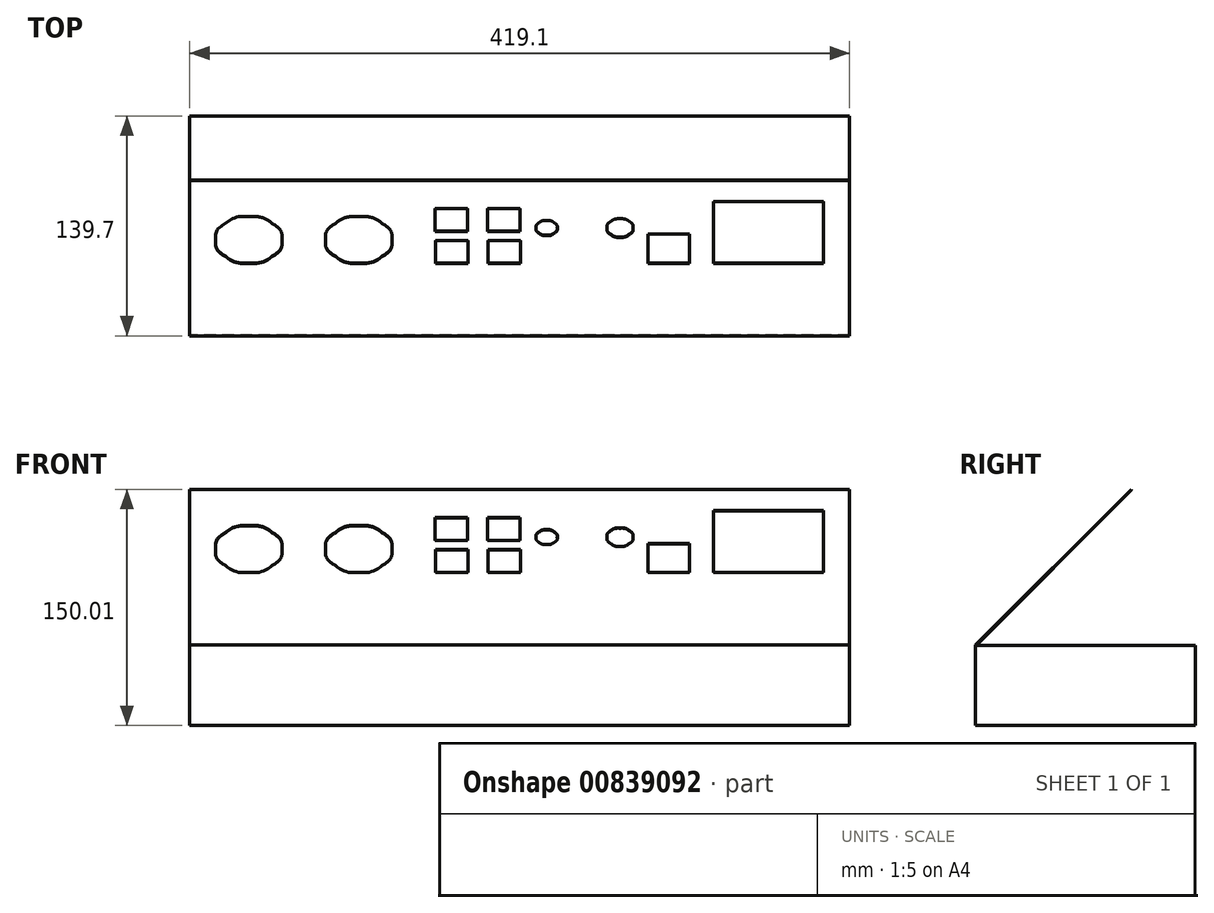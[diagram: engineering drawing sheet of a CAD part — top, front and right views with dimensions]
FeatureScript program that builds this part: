
annotation { "Feature Type Name" : "Feature", "Feature Type Description" : "" }
export const myFeature = defineFeature(function(context is Context, id is Id, definition is map)
    precondition{}
    {
        {
            var Q0;
            Q0=qCreatedBy(makeId("Right.planeOp"),FACE);
            var sketch = newSketch(context, id + "F0", { "sketchPlane" : qUnion([Q0])});
            skLineSegment(sketch, "E0.bottom", {"start": v(0, 0) * mm, "end": v(-139.7, 0) * mm});
            skLineSegment(sketch, "E0.top", {"start": v(0, 50.8) * mm, "end": v(-139.3, 50.8) * mm});
            skLineSegment(sketch, "E0.left", {"start": v(0, 0) * mm, "end": v(0, 50.8) * mm});
            skLineSegment(sketch, "E0.right", {"start": v(-139.7, 0) * mm, "end": v(-139.7, 51.22) * mm});
            skLineSegment(sketch, "E1", {"start": v(-139.7, 51.22) * mm, "end": v(-40.92, 150) * mm});
            skLineSegment(sketch, "E2", {"start": v(-40.92, 150) * mm, "end": v(-40.63, 149.72) * mm});
            skLineSegment(sketch, "E3", {"start": v(-40.63, 149.72) * mm, "end": v(-139.3, 51.05) * mm});
            skLineSegment(sketch, "E4", {"start": v(-139.3, 50.8) * mm, "end": v(-139.3, 51.05) * mm});
            skLineSegment(sketch, "E5", {"start": v(-139.3, 50.8) * mm, "end": v(-139.7, 50.8) * mm, "construction": true});
            skSolve(sketch);
        }
        {
            var Q0;
            Q0=qSketchRegion(id+"F0",true);
            extrude(context, id + "F1", {"entities" : qUnion([Q0]), "endBound" : BoundingType.SYMMETRIC, "depth" : 419.1 * mm, "offsetDistance" : 25.4 * mm});
        }
        {
            var Q0;
            Q0=makeQuery(id+"F1.opExtrude","SWEPT_FACE",FACE,{"disambiguationData":[OSD([sQuery(id+"F0.wireOp",EDGE,"E1")])]});
            var sketch = newSketch(context, id + "F2", { "sketchPlane" : qUnion([Q0])});
            skLineSegment(sketch, "E6", {"start": v(-32.8, 2.55) * mm, "end": v(-32.8, 23.19) * mm});
            skLineSegment(sketch, "E7", {"start": v(-32.8, 23.19) * mm, "end": v(-53.43, 23.19) * mm});
            skLineSegment(sketch, "E8", {"start": v(-53.43, 2.55) * mm, "end": v(-53.43, 23.19) * mm});
            skLineSegment(sketch, "E9", {"start": v(-53.43, 2.55) * mm, "end": v(-32.8, 2.55) * mm});
            skLineSegment(sketch, "E10", {"start": v(-53.83, 31.12) * mm, "end": v(-53.83, 51.76) * mm});
            skLineSegment(sketch, "E11", {"start": v(-53.83, 31.12) * mm, "end": v(-33.2, 31.12) * mm});
            skLineSegment(sketch, "E12", {"start": v(-33.2, 51.76) * mm, "end": v(-53.83, 51.76) * mm});
            skLineSegment(sketch, "E13", {"start": v(-33.2, 31.12) * mm, "end": v(-33.2, 51.76) * mm});
            skLineSegment(sketch, "E14", {"start": v(-20.1, 2.55) * mm, "end": v(0.54, 2.55) * mm});
            skLineSegment(sketch, "E15", {"start": v(-20.1, 2.55) * mm, "end": v(-20.1, 23.19) * mm});
            skLineSegment(sketch, "E16", {"start": v(0.54, 23.19) * mm, "end": v(-20.1, 23.19) * mm});
            skLineSegment(sketch, "E17", {"start": v(0.54, 2.55) * mm, "end": v(0.54, 23.19) * mm});
            skLineSegment(sketch, "E18", {"start": v(0.15, 31.12) * mm, "end": v(0.15, 51.76) * mm});
            skLineSegment(sketch, "E19", {"start": v(0.15, 51.76) * mm, "end": v(-20.5, 51.76) * mm});
            skLineSegment(sketch, "E20", {"start": v(-20.5, 31.12) * mm, "end": v(0.15, 31.12) * mm});
            skLineSegment(sketch, "E21", {"start": v(-20.5, 31.12) * mm, "end": v(-20.5, 51.76) * mm});
            skLineSegment(sketch, "E22", {"start": v(-210.2, -60.95) * mm, "end": v(-210.2, 77.96) * mm, "construction": true});
            skLineSegment(sketch, "E23", {"start": v(123.18, 2.55) * mm, "end": v(193.03, 2.55) * mm});
            skLineSegment(sketch, "E24", {"start": v(123.18, 58.11) * mm, "end": v(123.18, 2.55) * mm});
            skLineSegment(sketch, "E25", {"start": v(193.03, 58.11) * mm, "end": v(123.18, 58.11) * mm});
            skLineSegment(sketch, "E26", {"start": v(193.03, 2.55) * mm, "end": v(193.03, 58.11) * mm});
            skLineSegment(sketch, "E27", {"start": v(81.5, 2.55) * mm, "end": v(107.7, 2.55) * mm});
            skLineSegment(sketch, "E28", {"start": v(81.5, 28.74) * mm, "end": v(81.5, 2.55) * mm});
            skLineSegment(sketch, "E29", {"start": v(107.7, 28.74) * mm, "end": v(81.5, 28.74) * mm});
            skLineSegment(sketch, "E30", {"start": v(107.7, 2.55) * mm, "end": v(107.7, 28.74) * mm});
            skLineSegment(sketch, "E31", {"start": v(208.9, -60.95) * mm, "end": v(208.9, 77.96) * mm, "construction": true});
            skLineSegment(sketch, "E32", {"start": v(208.9, -60.95) * mm, "end": v(-210.2, -60.95) * mm, "construction": true});
            skLineSegment(sketch, "E33", {"start": v(-210.2, 77.96) * mm, "end": v(208.9, 77.96) * mm, "construction": true});
            skFitSpline(sketch, "E34", {"points": [v(17.06, 41.05) * mm, v(15.3, 41.05) * mm, v(13.54, 40.32) * mm, v(12.3, 39.07) * mm]});
            skFitSpline(sketch, "E35", {"points": [v(12.3, 39.07) * mm, v(11.05, 37.82) * mm, v(10.32, 36.07) * mm, v(10.32, 34.3) * mm, v(10.32, 32.53) * mm, v(11.05, 30.78) * mm, v(12.3, 29.53) * mm]});
            skFitSpline(sketch, "E36", {"points": [v(12.3, 29.53) * mm, v(13.54, 28.28) * mm, v(15.3, 27.55) * mm, v(17.06, 27.55) * mm, v(18.83, 27.55) * mm, v(20.59, 28.28) * mm, v(21.84, 29.53) * mm]});
            skFitSpline(sketch, "E37", {"points": [v(21.84, 29.53) * mm, v(23.08, 30.78) * mm, v(23.81, 32.53) * mm, v(23.81, 34.3) * mm, v(23.81, 36.07) * mm, v(23.08, 37.82) * mm, v(21.84, 39.07) * mm]});
            skFitSpline(sketch, "E38", {"points": [v(21.84, 39.07) * mm, v(20.59, 40.32) * mm, v(18.83, 41.05) * mm, v(17.06, 41.05) * mm]});
            skFitSpline(sketch, "E39", {"points": [v(-102.25, 44.62) * mm, v(-107.76, 44.62) * mm, v(-113.23, 42.35) * mm, v(-117.12, 38.46) * mm]});
            skFitSpline(sketch, "E40", {"points": [v(-117.12, 38.46) * mm, v(-121.02, 34.56) * mm, v(-123.28, 29.1) * mm, v(-123.28, 23.58) * mm, v(-123.28, 18.08) * mm, v(-121.02, 12.6) * mm, v(-117.12, 8.7) * mm]});
            skFitSpline(sketch, "E41", {"points": [v(-117.12, 8.7) * mm, v(-113.23, 4.82) * mm, v(-107.76, 2.55) * mm, v(-102.25, 2.55) * mm, v(-96.74, 2.55) * mm, v(-91.27, 4.82) * mm, v(-87.38, 8.7) * mm]});
            skFitSpline(sketch, "E42", {"points": [v(-87.38, 8.7) * mm, v(-83.48, 12.6) * mm, v(-81.21, 18.08) * mm, v(-81.21, 23.58) * mm, v(-81.21, 29.1) * mm, v(-83.48, 34.56) * mm, v(-87.38, 38.46) * mm]});
            skFitSpline(sketch, "E43", {"points": [v(-87.38, 38.46) * mm, v(-91.27, 42.35) * mm, v(-96.74, 44.62) * mm, v(-102.25, 44.62) * mm]});
            skFitSpline(sketch, "E44", {"points": [v(-172.1, 44.62) * mm, v(-177.6, 44.62) * mm, v(-183.08, 42.35) * mm, v(-186.97, 38.46) * mm, v(-190.87, 34.56) * mm, v(-193.13, 29.1) * mm, v(-193.13, 23.58) * mm, v(-193.13, 18.08) * mm, v(-190.87, 12.6) * mm, v(-186.97, 8.7) * mm]});
            skFitSpline(sketch, "E45", {"points": [v(-186.97, 8.7) * mm, v(-183.08, 4.82) * mm, v(-177.6, 2.55) * mm, v(-172.1, 2.55) * mm, v(-166.6, 2.55) * mm, v(-161.12, 4.82) * mm, v(-157.23, 8.7) * mm]});
            skFitSpline(sketch, "E46", {"points": [v(-157.23, 8.7) * mm, v(-153.33, 12.6) * mm, v(-151.06, 18.08) * mm, v(-151.06, 23.58) * mm, v(-151.06, 29.1) * mm, v(-153.33, 34.56) * mm, v(-157.23, 38.46) * mm]});
            skFitSpline(sketch, "E47", {"points": [v(-157.23, 38.46) * mm, v(-161.12, 42.35) * mm, v(-166.6, 44.62) * mm, v(-172.1, 44.62) * mm]});
            skFitSpline(sketch, "E48", {"points": [v(63.69, 42.63) * mm, v(61.5, 42.63) * mm, v(59.34, 41.74) * mm, v(57.8, 40.2) * mm]});
            skFitSpline(sketch, "E49", {"points": [v(57.8, 40.2) * mm, v(56.25, 38.65) * mm, v(55.36, 36.48) * mm, v(55.36, 34.3) * mm, v(55.36, 32.12) * mm, v(56.25, 29.95) * mm, v(57.8, 28.4) * mm]});
            skFitSpline(sketch, "E50", {"points": [v(57.8, 28.4) * mm, v(59.34, 26.86) * mm, v(61.5, 25.96) * mm, v(63.69, 25.96) * mm, v(65.87, 25.96) * mm, v(68.04, 26.86) * mm, v(69.58, 28.4) * mm]});
            skFitSpline(sketch, "E51", {"points": [v(69.58, 28.4) * mm, v(71.13, 29.95) * mm, v(72.02, 32.12) * mm, v(72.02, 34.3) * mm, v(72.02, 36.48) * mm, v(71.13, 38.65) * mm, v(69.58, 40.2) * mm]});
            skFitSpline(sketch, "E52", {"points": [v(69.58, 40.2) * mm, v(68.04, 41.74) * mm, v(65.87, 42.63) * mm, v(63.69, 42.63) * mm]});
            skSolve(sketch);
        }
        {
            var Q0;
            Q0=qSketchRegion(id+"F2",true);
            var Q1;
            Q1=makeQuery(id+"F1.opExtrude","SWEPT_FACE",FACE,{"disambiguationData":[OSD([sQuery(id+"F0.wireOp",EDGE,"E3")])]});
            extrude(context, id + "F3", {"entities" : qUnion([Q0]), "operationType" : NewBodyOperationType.REMOVE, "endBound" : BoundingType.UP_TO_SURFACE, "oppositeDirection" : true, "depth" : 25.4 * mm, "endBoundEntityFace" : qUnion([Q1]), "offsetDistance" : 25.4 * mm});
        }
    });
